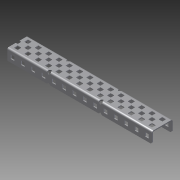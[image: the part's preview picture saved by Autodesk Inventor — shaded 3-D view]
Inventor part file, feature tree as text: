
AUTODESK INVENTOR PART (.ipt)
format: ipt  version: 2014 SP1 (Build 180222100, 222)  size: 973,312 bytes
history: native  units: in
note: dims shown in document units (in); Inventor stores cm internally (conversion verified against a paired STEP export)
features: other x1, imported_body x1, extrude x1, sketch x1
ambient origin geometry x8: Origin, YZ Plane, XZ Plane, XY Plane, X Axis, Y Axis, Z Axis, Center Point
bodies: Body1 (feature_tree)
feature tree (4):
  parser-record x1  (decoder bookkeeping rows leaked as tree rows — omitted from the tree; the rows remain in map.json)
  imported_body  "Base1"
  extrude  "Extrusion1"  Depth=0.5in TaperAngle=0.0deg
  sketch  "Sketch1"  dims[d0=0.5in d1=1.0in d2=0.0in]
